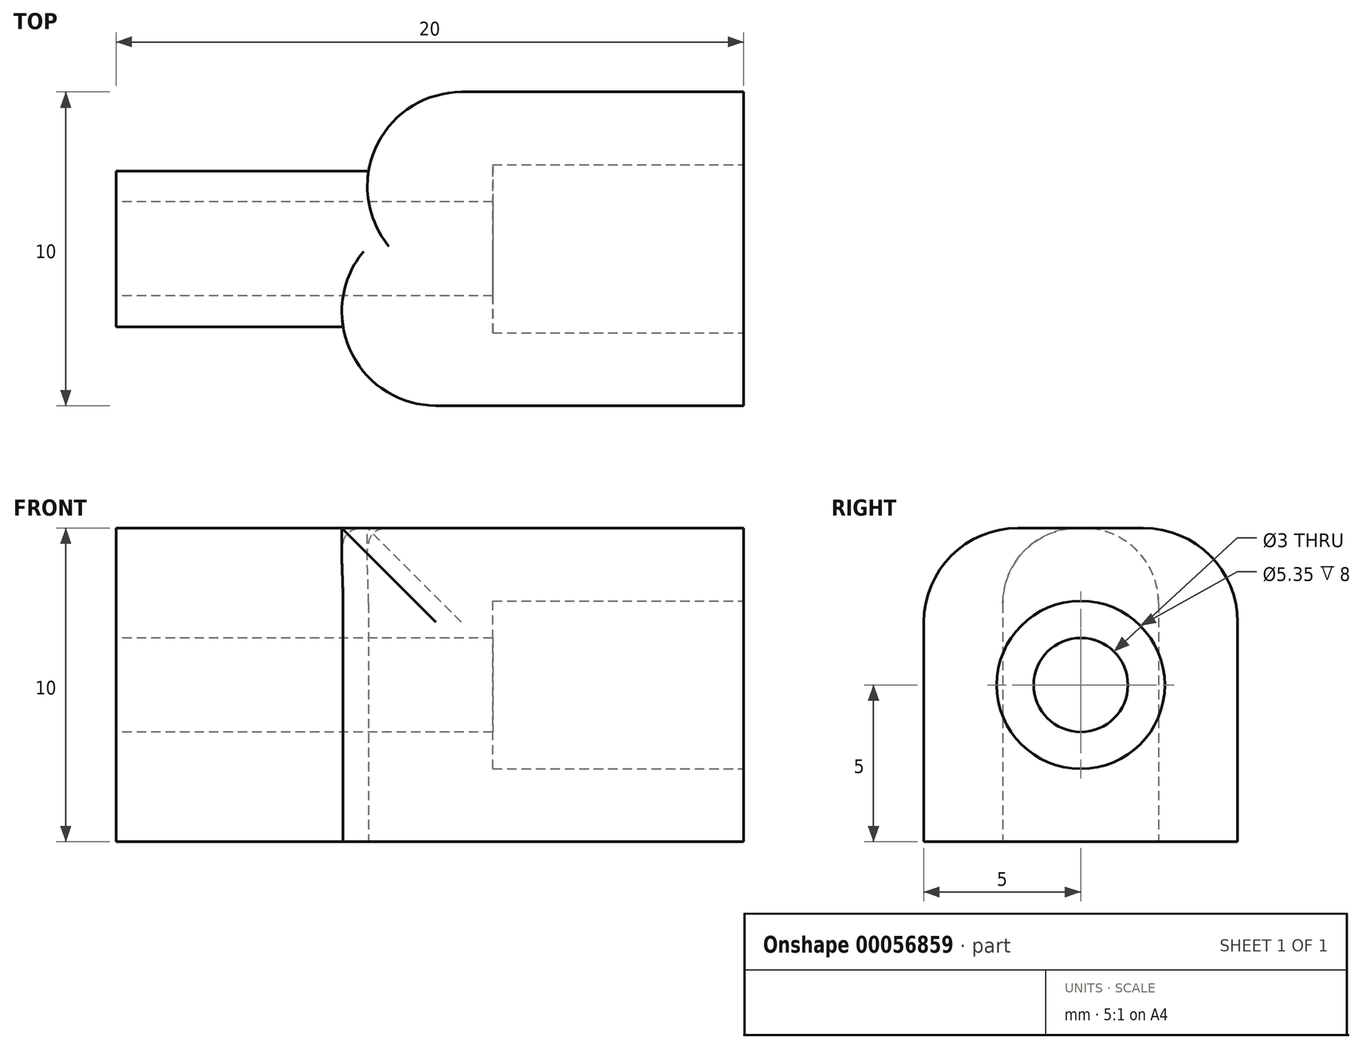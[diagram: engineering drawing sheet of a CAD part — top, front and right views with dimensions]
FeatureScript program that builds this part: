
annotation { "Feature Type Name" : "Feature", "Feature Type Description" : "" }
export const myFeature = defineFeature(function(context is Context, id is Id, definition is map)
    precondition{}
    {
        {
            var Q0;
            Q0=qCreatedBy(makeId("Top.planeOp"),FACE);
            var sketch = newSketch(context, id + "F0", { "sketchPlane" : qUnion([Q0])});
            skLineSegment(sketch, "E0", {"start": v(0, 5) * mm, "end": v(0, -5) * mm, "construction": true});
            skLineSegment(sketch, "E1", {"start": v(-10, 0) * mm, "end": v(10, 0) * mm, "construction": true});
            skLineSegment(sketch, "E2.0", {"start": v(-10, 5) * mm, "end": v(-10, -5) * mm, "construction": true});
            skLineSegment(sketch, "E3.0", {"start": v(10, 5) * mm, "end": v(10, -5) * mm, "construction": true});
            skLineSegment(sketch, "E4.0", {"start": v(-10, -5) * mm, "end": v(10, -5) * mm, "construction": true});
            skLineSegment(sketch, "E5.0", {"start": v(-10, 5) * mm, "end": v(10, 5) * mm, "construction": true});
            skPoint(sketch, "E6.orphan", {"position": v(0, 11.97) * mm});
            skPoint(sketch, "E7.orphan", {"position": v(-21.17, 0) * mm});
            skLineSegment(sketch, "E8", {"start": v(-10, 5) * mm, "end": v(10, 5) * mm});
            skLineSegment(sketch, "E9", {"start": v(10, -5) * mm, "end": v(10, 5) * mm});
            skLineSegment(sketch, "E10", {"start": v(10, -5) * mm, "end": v(-10, -5) * mm});
            skLineSegment(sketch, "E11", {"start": v(-10, 5) * mm, "end": v(-10, -5) * mm});
            skLineSegment(sketch, "E12", {"start": v(-10, 2.48) * mm, "end": v(0, 2.48) * mm});
            skLineSegment(sketch, "E13.MirrorCS", {"start": v(-10, -2.48) * mm, "end": v(0, -2.48) * mm});
            skLineSegment(sketch, "E14", {"start": v(-1.96, 5) * mm, "end": v(-1.96, 2.48) * mm});
            skLineSegment(sketch, "E15", {"start": v(-2.77, -2.48) * mm, "end": v(-2.77, -5) * mm});
            skSolve(sketch);
        }
        {
            var Q0;
            {var subQ6=sQuery(id+"F0.wireOp",EDGE,"E9");Q0=makeQuery(id+"F0.imprint","IMPRINT",FACE,{"disambiguationData":[TD([[makeQuery(id+"F0.imprint","IMPRINT",EDGE,{"derivedFrom":subQ6}),1.0]])]});}
            extrude(context, id + "F1", {"entities" : qUnion([Q0]), "depth" : 10 * mm});
        }
        {
            var Q0;
            Q0=makeQuery(id+"F1.opExtrude","SWEPT_FACE",FACE,{"disambiguationData":[OSD([sQuery(id+"F0.wireOp",EDGE,"E11")])]});
            var sketch = newSketch(context, id + "F2", { "sketchPlane" : qUnion([Q0])});
            skLineSegment(sketch, "E16", {"start": v(-2.48, 5) * mm, "end": v(2.48, 5) * mm, "construction": true});
            skCircle(sketch, "E17", {"center": v(0, 5) * mm, "radius": 1.5 * mm});
            skSolve(sketch);
        }
        {
            var Q0;
            Q0=makeQuery(id+"F2.imprint","IMPRINT",FACE,{"disambiguationData":[TD([[makeQuery(id+"F2.imprint","IMPRINT",EDGE,{"derivedFrom":sQuery(id+"F2.wireOp",EDGE,"E17")}),1.0]])]});
            extrude(context, id + "F3", {"entities" : qUnion([Q0]), "operationType" : NewBodyOperationType.REMOVE, "oppositeDirection" : true, "depth" : 25 * mm});
        }
        {
            var Q0;
            Q0=makeQuery(id+"F1.opExtrude","SWEPT_FACE",FACE,{"disambiguationData":[OSD([sQuery(id+"F0.wireOp",EDGE,"E9")])]});
            var sketch = newSketch(context, id + "F4", { "sketchPlane" : qUnion([Q0])});
            skCircle(sketch, "E18", {"center": v(0, 5) * mm, "radius": 2.68 * mm});
            skSolve(sketch);
        }
        {
            var Q0;
            Q0=makeQuery(id+"F4.imprint","IMPRINT",FACE,{"disambiguationData":[TD([[makeQuery(id+"F4.imprint","IMPRINT",EDGE,{"derivedFrom":sQuery(id+"F4.wireOp",EDGE,"E18")}),1.0]])]});
            extrude(context, id + "F5", {"entities" : qUnion([Q0]), "operationType" : NewBodyOperationType.REMOVE, "oppositeDirection" : true, "depth" : 8 * mm});
        }
        {
            var Q0;
            Q0=makeQuery(id+"F1.opExtrude","CAP_EDGE",EDGE,{"disambiguationData":[OSD([sQuery(id+"F0.wireOp",EDGE,"E10")])],"isStart":false});
            var Q1;
            Q1=makeQuery(id+"F1.opExtrude","CAP_EDGE",EDGE,{"disambiguationData":[OSD([sQuery(id+"F0.wireOp",EDGE,"E8")])],"isStart":false});
            var Q2;
            Q2=makeQuery(id+"F1.opExtrude","SWEPT_EDGE",EDGE,{"disambiguationData":[OSD([sQuery(id+"F0.wireOp",EDGE,"E10"),sQuery(id+"F0.wireOp",EDGE,"E15")])]});
            var Q3;
            Q3=makeQuery(id+"F1.opExtrude","SWEPT_EDGE",EDGE,{"disambiguationData":[OSD([sQuery(id+"F0.wireOp",EDGE,"E8"),sQuery(id+"F0.wireOp",EDGE,"E14")])]});
            fillet(context, id + "F6", {"entities" : qUnion([Q0, Q1, Q2, Q3]), "radius" : 3 * mm, "tangentPropagation" : true, "allowEdgeOverflow" : false});
        }
        {
            var Q0;
            Q0=makeQuery(id+"F6.opFillet","BLEND_EDGE",EDGE,{"blendedFrom":[makeQuery(id+"F1.opExtrude","CAP_EDGE",EDGE,{"disambiguationData":[OSD([sQuery(id+"F0.wireOp",EDGE,"E10")])],"isStart":false}),makeQuery(id+"F1.opExtrude","SWEPT_FACE",FACE,{"disambiguationData":[OSD([sQuery(id+"F0.wireOp",EDGE,"E13.MirrorCS")])]})],"blendedInto":[makeQuery(id+"F1.opExtrude","SWEPT_FACE",FACE,{"disambiguationData":[OSD([sQuery(id+"F0.wireOp",EDGE,"E13.MirrorCS")])]})]});
            var Q1;
            Q1=makeQuery(id+"F6.opFillet","BLEND_EDGE",EDGE,{"blendedFrom":[makeQuery(id+"F1.opExtrude","CAP_EDGE",EDGE,{"disambiguationData":[OSD([sQuery(id+"F0.wireOp",EDGE,"E8")])],"isStart":false}),makeQuery(id+"F1.opExtrude","SWEPT_FACE",FACE,{"disambiguationData":[OSD([sQuery(id+"F0.wireOp",EDGE,"E12")])]})],"blendedInto":[makeQuery(id+"F1.opExtrude","SWEPT_FACE",FACE,{"disambiguationData":[OSD([sQuery(id+"F0.wireOp",EDGE,"E12")])]})]});
            fillet(context, id + "F7", {"entities" : qUnion([Q0, Q1]), "radius" : 2.4 * mm, "tangentPropagation" : true, "allowEdgeOverflow" : false});
        }
    });
